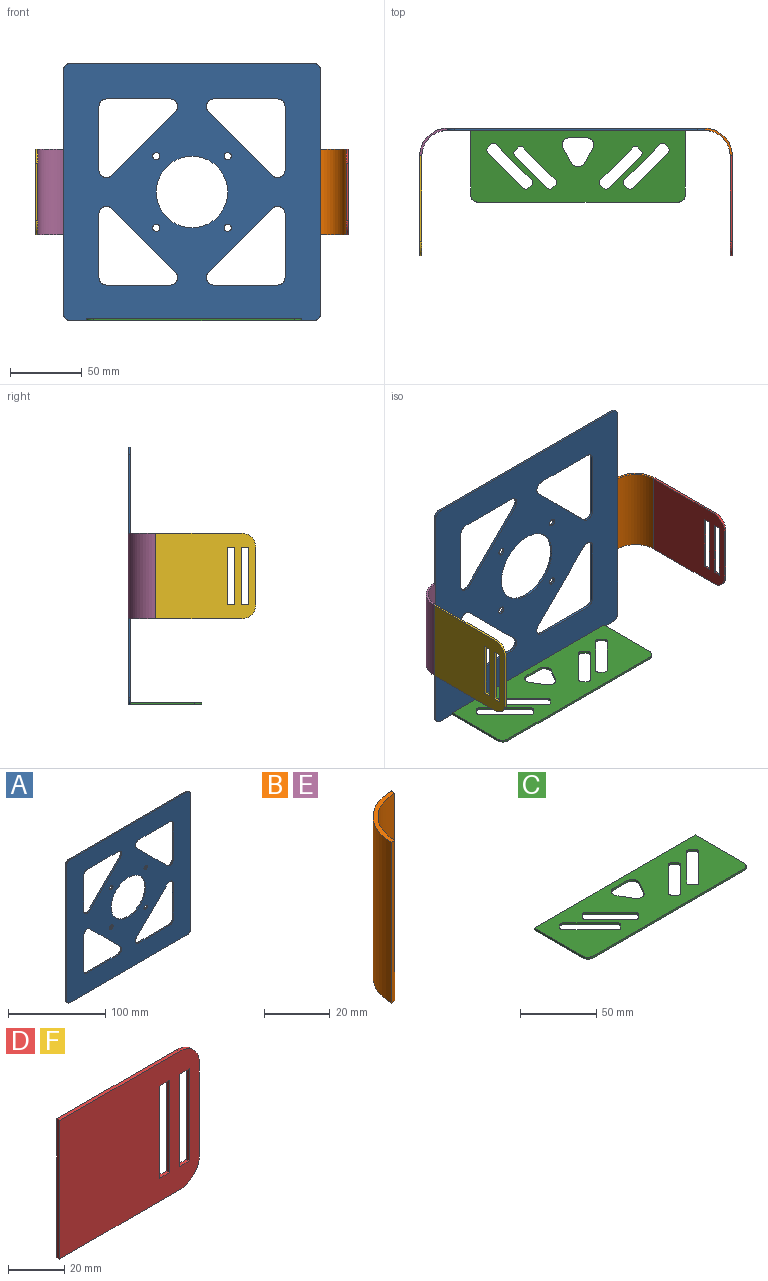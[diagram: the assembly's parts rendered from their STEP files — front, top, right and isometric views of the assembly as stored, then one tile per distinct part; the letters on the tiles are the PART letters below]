
ASSEMBLY  parts=6 mates=6
PART A: 39 faces, bbox 180x1.5x180 mm
  f0: plane 45x45mm, normal (0.71,0,0.71), area 95.5mm2, adj f1,f27,f37,f38
  f1: cylinder r=5mm len=8.54mm, axis (0,1,0), area 17.7mm2, adj f0,f2,f37,f38
  f2: plane 45x1.5mm, normal (0,0,-1), area 67.5mm2, adj f1,f3,f37,f38
  f3: cylinder r=5mm len=5mm, axis (0,1,0), area 11.8mm2, adj f2,f4,f37,f38
  f4: plane 45x1.5mm, normal (-1,0,0), area 67.5mm2, adj f3,f27,f37,f38
  f5: plane 45x45mm, normal (-0.71,0,-0.71), area 95.5mm2, adj f6,f28,f37,f38
  f6: cylinder r=5mm len=8.54mm, axis (0,1,0), area 17.7mm2, adj f5,f7,f37,f38
  f7: plane 45x1.5mm, normal (0,0,1), area 67.5mm2, adj f6,f8,f37,f38
  f8: cylinder r=5mm len=5mm, axis (0,1,0), area 11.8mm2, adj f7,f9,f37,f38
  f9: plane 45x1.5mm, normal (1,0,0), area 67.5mm2, adj f8,f28,f37,f38
  f10: plane 170x1.5mm, normal (0,0,1), area 255mm2, adj f11,f29,f37,f38
  f11: cylinder r=5mm len=5mm, axis (0,1,0), area 11.8mm2, adj f10,f12,f37,f38
  f12: plane 170x1.5mm, normal (-1,0,0), area 255mm2, adj f11,f13,f37,f38
  f13: cylinder r=5mm len=5mm, axis (0,1,0), area 11.8mm2, adj f12,f14,f37,f38
  f14: plane 170x1.5mm, normal (0,0,-1), area 255mm2, adj f13,f15,f37,f38
  f15: cylinder r=5mm len=5mm, axis (0,1,0), area 11.8mm2, adj f14,f16,f37,f38
  f16: plane 170x1.5mm, normal (1,0,0), area 255mm2, adj f15,f29,f37,f38
  f17: cylinder r=5mm len=8.54mm, axis (0,1,0), area 17.7mm2, adj f18,f30,f37,f38
  f18: plane 45x1.5mm, normal (1,0,0), area 67.5mm2, adj f17,f19,f37,f38
  f19: cylinder r=5mm len=5mm, axis (0,1,0), area 11.8mm2, adj f18,f20,f37,f38
  f20: plane 45x1.5mm, normal (0,0,-1), area 67.5mm2, adj f19,f21,f37,f38
  f21: cylinder r=5mm len=8.54mm, axis (0,1,0), area 17.7mm2, adj f20,f30,f37,f38
  f22: cylinder r=5mm len=8.54mm, axis (0,1,0), area 17.7mm2, adj f23,f31,f37,f38
  f23: plane 45x45mm, normal (0.71,0,-0.71), area 95.5mm2, adj f22,f24,f37,f38
  f24: cylinder r=5mm len=8.54mm, axis (0,1,0), area 17.7mm2, adj f23,f25,f37,f38
  f25: plane 45x1.5mm, normal (-1,0,0), area 67.5mm2, adj f24,f26,f37,f38
  f26: cylinder r=5mm len=5mm, axis (0,1,0), area 11.8mm2, adj f25,f31,f37,f38
  f27: cylinder r=5mm len=8.54mm, axis (0,1,0), area 17.7mm2, adj f0,f4,f37,f38
  f28: cylinder r=5mm len=8.54mm, axis (0,1,0), area 17.7mm2, adj f5,f9,f37,f38
  f29: cylinder r=5mm len=5mm, axis (0,1,0), area 11.8mm2, adj f10,f16,f37,f38
  f30: plane 45x45mm, normal (-0.71,0,0.71), area 95.5mm2, adj f17,f21,f37,f38
  f31: plane 45x1.5mm, normal (0,0,1), area 67.5mm2, adj f22,f26,f37,f38
  f32: cylinder r=25mm len=50mm, axis (0,1,0), area 235.6mm2, adj f37,f38
  f33: cylinder r=2.5mm len=5mm, axis (0,1,0), area 23.6mm2, adj f37,f38
  f34: cylinder r=2.5mm len=5mm, axis (0,1,0), area 23.6mm2, adj f37,f38
  f35: cylinder r=2.5mm len=5mm, axis (0,1,0), area 23.6mm2, adj f37,f38
  f36: cylinder r=2.5mm len=5mm, axis (0,1,0), area 23.6mm2, adj f37,f38
  f37: plane 180x180mm, normal (0,-1,0), area 22899.6mm2, adj f0,f1,f2,f3,f4,f5,f6,f7
  f38: plane 180x180mm, normal (0,1,0), area 22899.6mm2, adj f0,f1,f2,f3,f4,f5,f6,f7
PART B: 6 faces, bbox 19.2x19.2x60 mm
  f0: plane 60x1.5mm, normal (1,0,0), area 90mm2, adj f1,f3,f4,f5
  f1: cylinder r=19.18mm len=60mm, axis (0,0,1), area 1807.5mm2, adj f0,f2,f4,f5
  f2: plane 60x1.5mm, normal (0,-1,0), area 90mm2, adj f1,f3,f4,f5
  f3: cylinder r=17.68mm len=60mm, axis (0,0,1), area 1666.1mm2, adj f0,f2,f4,f5
  f4: plane 19.18x19.18mm, normal (0,0,-1), area 43.4mm2, adj f0,f1,f2,f3
  f5: plane 19.18x19.18mm, normal (0,0,1), area 43.4mm2, adj f0,f1,f2,f3
PART C: 46 faces, bbox 150x50x1.5 mm
  f0: cylinder r=2mm len=2.83mm, axis (0,0,-1), area 4.7mm2, adj f1,f43,f44,f45
  f1: plane 25.36x25.36mm, normal (-0.71,0.71,0), area 53.8mm2, adj f0,f2,f44,f45
  f2: cylinder r=2mm len=2.83mm, axis (0,0,-1), area 4.7mm2, adj f1,f3,f44,f45
  f3: plane 2.84x2.84mm, normal (0.71,0.71,0), area 6mm2, adj f2,f4,f44,f45
  f4: cylinder r=2mm len=2.83mm, axis (0,0,-1), area 4.7mm2, adj f3,f5,f44,f45
  f5: plane 25.36x25.36mm, normal (0.71,-0.71,0), area 53.8mm2, adj f4,f6,f44,f45
  f6: cylinder r=2mm len=2.83mm, axis (0,0,-1), area 4.7mm2, adj f5,f43,f44,f45
  f7: cylinder r=2mm len=2.83mm, axis (0,0,-1), area 4.7mm2, adj f8,f38,f44,f45
  f8: plane 23.24x23.24mm, normal (-0.71,0.71,0), area 49.3mm2, adj f7,f9,f44,f45
  f9: cylinder r=2mm len=2.83mm, axis (0,0,-1), area 4.7mm2, adj f8,f10,f44,f45
  f10: plane 2.84x2.84mm, normal (0.71,0.71,0), area 6mm2, adj f9,f11,f44,f45
  f11: cylinder r=2mm len=2.83mm, axis (0,0,-1), area 4.7mm2, adj f10,f12,f44,f45
  f12: plane 23.24x23.24mm, normal (0.71,-0.71,0), area 49.3mm2, adj f11,f13,f44,f45
  f13: cylinder r=2mm len=2.83mm, axis (0,0,-1), area 4.7mm2, adj f12,f38,f44,f45
  f14: plane 150x1.5mm, normal (0,1,0), area 225mm2, adj f15,f39,f44,f45
  f15: plane 45x1.5mm, normal (-1,0,0), area 67.5mm2, adj f14,f16,f44,f45
  f16: cylinder r=5mm len=5mm, axis (0,0,-1), area 11.8mm2, adj f15,f17,f44,f45
  f17: plane 140x1.5mm, normal (0,-1,0), area 210mm2, adj f16,f18,f44,f45
  f18: cylinder r=5mm len=5mm, axis (0,0,-1), area 11.8mm2, adj f17,f39,f44,f45
  f19: cylinder r=5mm len=8.58mm, axis (0,0,-1), area 15.5mm2, adj f20,f40,f44,f45
  f20: plane 10.28x6.17mm, normal (0.86,0.51,0), area 18mm2, adj f19,f21,f44,f45
  f21: cylinder r=5mm len=7.57mm, axis (0,0,-1), area 15.8mm2, adj f20,f22,f44,f45
  f22: plane 12.34x1.5mm, normal (0,-1,0), area 18.5mm2, adj f21,f23,f44,f45
  f23: cylinder r=5mm len=7.57mm, axis (0,0,-1), area 15.8mm2, adj f22,f40,f44,f45
  f24: plane 23.24x23.24mm, normal (0.71,0.71,0), area 49.3mm2, adj f25,f41,f44,f45
  f25: cylinder r=2mm len=2.83mm, axis (0,0,-1), area 4.7mm2, adj f24,f26,f44,f45
  f26: plane 2.84x2.84mm, normal (0.71,-0.71,0), area 6mm2, adj f25,f27,f44,f45
  f27: cylinder r=2mm len=2.83mm, axis (0,0,-1), area 4.7mm2, adj f26,f28,f44,f45
  f28: plane 23.24x23.24mm, normal (-0.71,-0.71,0), area 49.3mm2, adj f27,f29,f44,f45
  f29: cylinder r=2mm len=2.83mm, axis (0,0,-1), area 4.7mm2, adj f28,f30,f44,f45
  f30: plane 2.84x2.84mm, normal (-0.71,0.71,0), area 6mm2, adj f29,f41,f44,f45
  f31: plane 25.36x25.36mm, normal (0.71,0.71,0), area 53.8mm2, adj f32,f42,f44,f45
  f32: cylinder r=2mm len=2.83mm, axis (0,0,-1), area 4.7mm2, adj f31,f33,f44,f45
  f33: plane 2.84x2.84mm, normal (0.71,-0.71,0), area 6mm2, adj f32,f34,f44,f45
  f34: cylinder r=2mm len=2.83mm, axis (0,0,-1), area 4.7mm2, adj f33,f35,f44,f45
  f35: plane 25.36x25.36mm, normal (-0.71,-0.71,0), area 53.8mm2, adj f34,f36,f44,f45
  f36: cylinder r=2mm len=2.83mm, axis (0,0,-1), area 4.7mm2, adj f35,f37,f44,f45
  f37: plane 2.84x2.84mm, normal (-0.71,0.71,0), area 6mm2, adj f36,f42,f44,f45
  f38: plane 2.84x2.84mm, normal (-0.71,-0.71,0), area 6mm2, adj f7,f13,f44,f45
  f39: plane 45x1.5mm, normal (1,0,0), area 67.5mm2, adj f14,f18,f44,f45
  f40: plane 10.28x6.17mm, normal (-0.86,0.51,0), area 18mm2, adj f19,f23,f44,f45
  f41: cylinder r=2mm len=2.83mm, axis (0,0,-1), area 4.7mm2, adj f24,f30,f44,f45
  f42: cylinder r=2mm len=2.83mm, axis (0,0,-1), area 4.7mm2, adj f31,f37,f44,f45
  f43: plane 2.84x2.84mm, normal (-0.71,-0.71,0), area 6mm2, adj f0,f6,f44,f45
  f44: plane 150x50mm, normal (0,0,1), area 5950mm2, adj f0,f1,f2,f3,f4,f5,f6,f7
  f45: plane 150x50mm, normal (0,0,-1), area 5950mm2, adj f0,f1,f2,f3,f4,f5,f6,f7
PART D: 16 faces, bbox 70x1.5x60 mm
  f0: plane 40x1.5mm, normal (-1,0,0), area 60mm2, adj f1,f13,f14,f15
  f1: plane 5x1.5mm, normal (0,0,1), area 7.5mm2, adj f0,f2,f14,f15
  f2: plane 40x1.5mm, normal (1,0,0), area 60mm2, adj f1,f13,f14,f15
  f3: plane 40x1.5mm, normal (-1,0,0), area 60mm2, adj f4,f11,f14,f15
  f4: plane 5x1.5mm, normal (0,0,1), area 7.5mm2, adj f3,f5,f14,f15
  f5: plane 40x1.5mm, normal (1,0,0), area 60mm2, adj f4,f11,f14,f15
  f6: plane 40x1.5mm, normal (1,0,0), area 60mm2, adj f7,f12,f14,f15
  f7: cylinder r=10mm len=10mm, axis (0,1,0), area 23.6mm2, adj f6,f8,f14,f15
  f8: plane 60x1.5mm, normal (0,0,1), area 90mm2, adj f7,f9,f14,f15
  f9: plane 60x1.5mm, normal (-1,0,0), area 90mm2, adj f8,f10,f14,f15
  f10: plane 60x1.5mm, normal (0,0,-1), area 90mm2, adj f9,f12,f14,f15
  f11: plane 5x1.5mm, normal (0,0,-1), area 7.5mm2, adj f3,f5,f14,f15
  f12: cylinder r=10mm len=10mm, axis (0,1,0), area 23.6mm2, adj f6,f10,f14,f15
  f13: plane 5x1.5mm, normal (0,0,-1), area 7.5mm2, adj f0,f2,f14,f15
  f14: plane 70x60mm, normal (0,-1,0), area 3757.1mm2, adj f0,f1,f2,f3,f4,f5,f6,f7
  f15: plane 70x60mm, normal (0,1,0), area 3757.1mm2, adj f0,f1,f2,f3,f4,f5,f6,f7
PART E: same geometry as B
PART F: same geometry as D
PLACE A t=(-116.47,-189.76,-174.88)mm
PLACE B rot(axis=(0,0,-1),90deg) t=(82.71,-208.93,-114.88)mm
PLACE C t=(-100.08,-241.26,-174.88)mm
PLACE D rot(axis=(0,0,-1),90deg) t=(82.71,-208.93,-114.88)mm
PLACE E rot(axis=(0.71,-0.71,0),180deg) t=(-135.64,-208.93,-54.88)mm
PLACE F rot(axis=(0,0,-1),90deg) t=(-134.14,-208.93,-114.88)mm
MATE planar C.f45 <-> A.f14  axis (0,0,-1) through (-31.24,-196.26,-174.88)mm
MATE planar B.f2 <-> A.f16  axis (-1,0,0) through (63.53,-190.51,-84.88)mm
MATE planar C.f14 <-> A.f15  axis (0,1,0) through (49.92,-191.26,-174.13)mm
MATE planar F.f9 <-> E.f0  axis (0,1,0) through (-134.89,-208.93,-54.88)mm
MATE planar E.f2 <-> A.f12  axis (1,0,0) through (-116.47,-190.51,-84.88)mm
MATE planar D.f9 <-> B.f0  axis (0,1,0) through (81.96,-208.93,-54.88)mm
